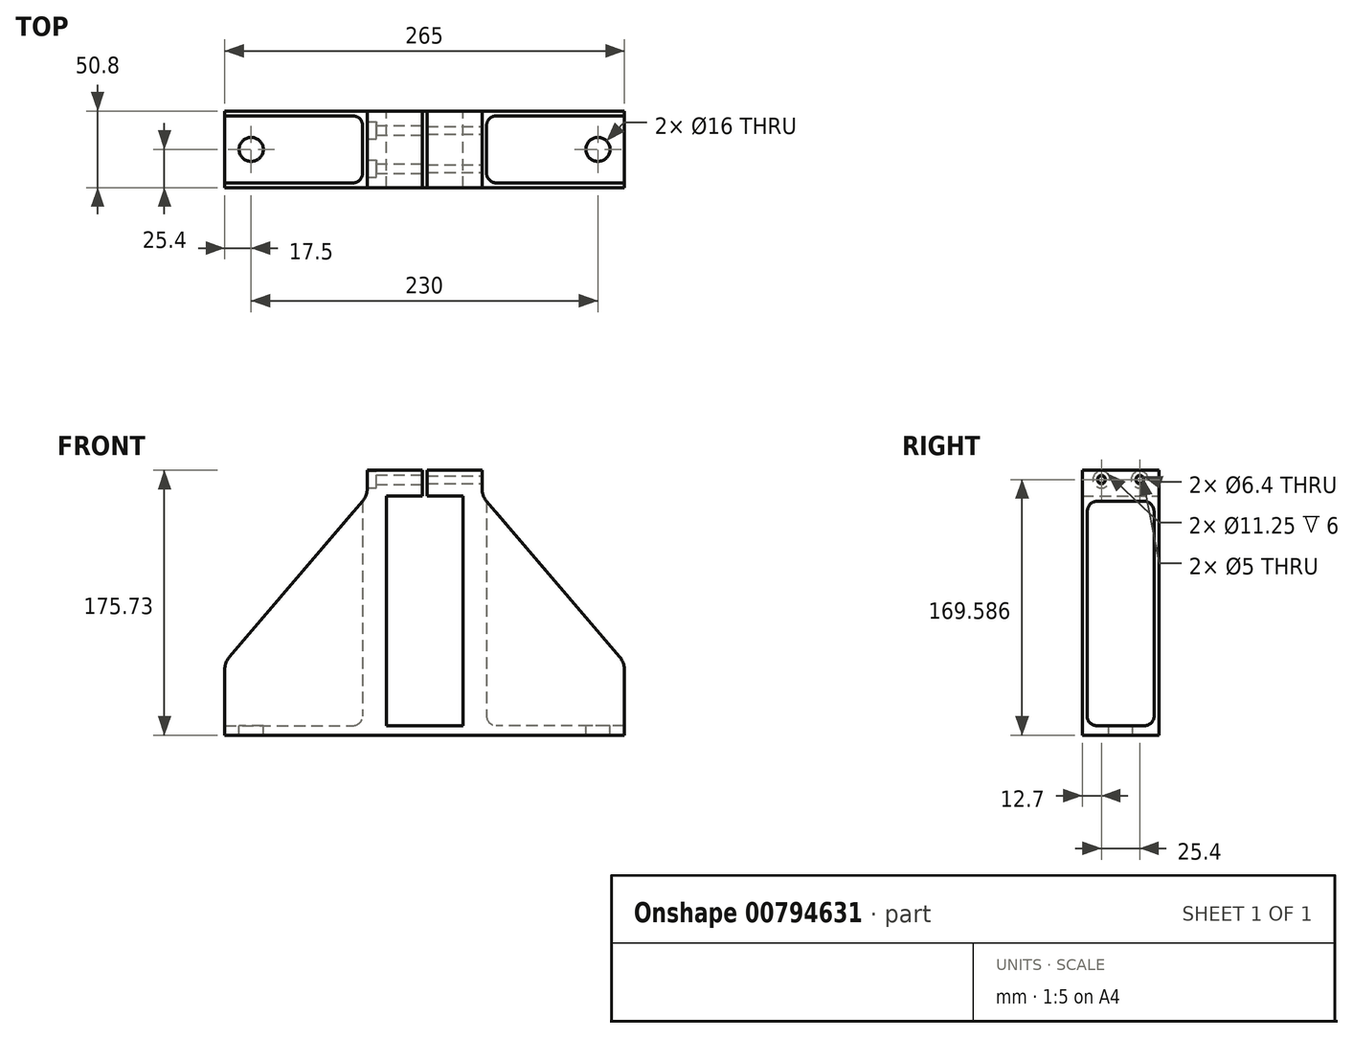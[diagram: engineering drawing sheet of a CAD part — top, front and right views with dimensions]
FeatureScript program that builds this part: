
annotation { "Feature Type Name" : "Feature", "Feature Type Description" : "" }
export const myFeature = defineFeature(function(context is Context, id is Id, definition is map)
    precondition{}
    {
        {
            var Q0;
            Q0=qCreatedBy(makeId("Front.planeOp"),FACE);
            var sketch = newSketch(context, id + "F0", { "sketchPlane" : qUnion([Q0])});
            skLineSegment(sketch, "E0.bottom", {"start": v(25.4, -76.2) * mm, "end": v(-25.4, -76.2) * mm, "construction": true});
            skLineSegment(sketch, "E0.top", {"start": v(25.4, 76.2) * mm, "end": v(1.59, 76.2) * mm, "construction": true});
            skLineSegment(sketch, "E0.left", {"start": v(25.4, -76.2) * mm, "end": v(25.4, 76.2) * mm, "construction": true});
            skLineSegment(sketch, "E0.right", {"start": v(-25.4, -76.2) * mm, "end": v(-25.4, 76.2) * mm, "construction": true});
            skPoint(sketch, "E0.middle", {"position": v(0, 0) * mm});
            skLineSegment(sketch, "E1.bottom", {"start": v(22.22, -73.03) * mm, "end": v(-22.23, -73.03) * mm, "construction": true});
            skLineSegment(sketch, "E1.top", {"start": v(22.23, 73.03) * mm, "end": v(-22.22, 73.03) * mm, "construction": true});
            skLineSegment(sketch, "E1.left", {"start": v(22.22, -73.03) * mm, "end": v(22.23, 73.02) * mm, "construction": true});
            skLineSegment(sketch, "E1.right", {"start": v(-22.23, -73.02) * mm, "end": v(-22.22, 73.03) * mm, "construction": true});
            skLineSegment(sketch, "E2", {"start": v(-115, -34.18) * mm, "end": v(-115, -125.66) * mm, "construction": true});
            skLineSegment(sketch, "E3", {"start": v(115, -25.79) * mm, "end": v(115, -125.66) * mm, "construction": true});
            skLineSegment(sketch, "E4", {"start": v(-43.18, -85.2) * mm, "end": v(50.09, -85.2) * mm, "construction": true});
            skLineSegment(sketch, "E5", {"start": v(50.09, -104.25) * mm, "end": v(-46.8, -104.25) * mm, "construction": true});
            skLineSegment(sketch, "E6", {"start": v(50.09, -85.2) * mm, "end": v(50.09, -104.25) * mm, "construction": true});
            skPoint(sketch, "E7", {"position": v(115, -94.72) * mm});
            skPoint(sketch, "E7.positionSnap0", {"position": v(50.09, -94.72) * mm});
            skLineSegment(sketch, "E8.bottom", {"start": v(132.5, -103.72) * mm, "end": v(97.5, -103.72) * mm, "construction": true});
            skLineSegment(sketch, "E8.top", {"start": v(132.5, -85.72) * mm, "end": v(97.5, -85.72) * mm, "construction": true});
            skLineSegment(sketch, "E8.left", {"start": v(132.5, -103.72) * mm, "end": v(132.5, -85.72) * mm, "construction": true});
            skLineSegment(sketch, "E8.right", {"start": v(97.5, -103.72) * mm, "end": v(97.5, -85.72) * mm, "construction": true});
            skPoint(sketch, "E9", {"position": v(-115, -94.72) * mm});
            skLineSegment(sketch, "E10.bottom", {"start": v(-97.5, -103.72) * mm, "end": v(-132.5, -103.72) * mm, "construction": true});
            skLineSegment(sketch, "E10.top", {"start": v(-97.5, -85.72) * mm, "end": v(-132.5, -85.72) * mm, "construction": true});
            skLineSegment(sketch, "E10.left", {"start": v(-97.5, -103.72) * mm, "end": v(-97.5, -85.72) * mm, "construction": true});
            skLineSegment(sketch, "E10.right", {"start": v(-132.5, -103.72) * mm, "end": v(-132.5, -85.72) * mm, "construction": true});
            skLineSegment(sketch, "E11", {"start": v(107, -85.72) * mm, "end": v(107, -53.22) * mm, "construction": true});
            skLineSegment(sketch, "E12", {"start": v(107, -53.22) * mm, "end": v(123, -53.22) * mm, "construction": true});
            skLineSegment(sketch, "E13", {"start": v(123, -53.22) * mm, "end": v(123, -85.72) * mm, "construction": true});
            skPoint(sketch, "E14", {"position": v(-115, -69.47) * mm});
            skLineSegment(sketch, "E15.bottom", {"start": v(-107, -85.72) * mm, "end": v(-123, -85.72) * mm, "construction": true});
            skLineSegment(sketch, "E15.top", {"start": v(-107, -53.22) * mm, "end": v(-123, -53.22) * mm, "construction": true});
            skLineSegment(sketch, "E15.left", {"start": v(-107, -85.72) * mm, "end": v(-107, -53.22) * mm, "construction": true});
            skLineSegment(sketch, "E15.right", {"start": v(-123, -85.72) * mm, "end": v(-123, -53.22) * mm, "construction": true});
            skLineSegment(sketch, "E16.bottom", {"start": v(-132.5, -82.55) * mm, "end": v(132.5, -82.55) * mm});
            skLineSegment(sketch, "E16.top", {"start": v(-38.1, 93.18) * mm, "end": v(-1.59, 93.18) * mm});
            skLineSegment(sketch, "E16.left", {"start": v(-132.5, -82.55) * mm, "end": v(-132.5, -38.87) * mm});
            skLineSegment(sketch, "E16.right", {"start": v(132.5, -82.55) * mm, "end": v(132.5, -38.87) * mm});
            skLineSegment(sketch, "E17.bottom", {"start": v(-25.4, 76.2) * mm, "end": v(-1.59, 76.2) * mm});
            skLineSegment(sketch, "E17.top", {"start": v(-25.4, -76.2) * mm, "end": v(25.4, -76.2) * mm});
            skLineSegment(sketch, "E17.left", {"start": v(-25.4, 76.2) * mm, "end": v(-25.4, -76.2) * mm});
            skLineSegment(sketch, "E17.right", {"start": v(25.4, 76.2) * mm, "end": v(25.4, -76.2) * mm});
            skLineSegment(sketch, "E18", {"start": v(-129.45, -30.61) * mm, "end": v(-41.15, 72.64) * mm});
            skLineSegment(sketch, "E19", {"start": v(-38.1, 80.9) * mm, "end": v(-38.1, 93.18) * mm});
            skLineSegment(sketch, "E20", {"start": v(38.1, 93.18) * mm, "end": v(38.1, 80.9) * mm});
            skLineSegment(sketch, "E21", {"start": v(41.15, 72.64) * mm, "end": v(129.45, -30.61) * mm});
            skLineSegment(sketch, "E22", {"start": v(0, 76.2) * mm, "end": v(0, 93.18) * mm, "construction": true});
            skLineSegment(sketch, "E23.left", {"start": v(1.59, 76.2) * mm, "end": v(1.59, 93.18) * mm});
            skLineSegment(sketch, "E23.right", {"start": v(-1.59, 76.2) * mm, "end": v(-1.59, 93.18) * mm});
            skPoint(sketch, "E23.middle", {"position": v(0, 84.7) * mm});
            skLineSegment(sketch, "E24.trimOffspring", {"start": v(1.59, 93.18) * mm, "end": v(38.1, 93.18) * mm});
            skLineSegment(sketch, "E25.trimOffspring", {"start": v(-1.59, 76.2) * mm, "end": v(-25.4, 76.2) * mm, "construction": true});
            skLineSegment(sketch, "E26.trimOffspring", {"start": v(1.59, 76.2) * mm, "end": v(25.4, 76.2) * mm});
            skPoint(sketch, "E27.visualSharp", {"position": v(-38.1, 76.2) * mm});
            skArc(sketch, "E27.filletArc", {"start": v(-41.15, 72.64) * mm, "mid": v(-38.89, 76.5) * mm, "end": v(-38.1, 80.9) * mm});
            skPoint(sketch, "E28.visualSharp", {"position": v(38.1, 76.2) * mm});
            skArc(sketch, "E28.filletArc", {"start": v(38.1, 80.9) * mm, "mid": v(38.89, 76.5) * mm, "end": v(41.15, 72.64) * mm});
            skPoint(sketch, "E29.visualSharp", {"position": v(-132.5, -34.17) * mm});
            skArc(sketch, "E29.filletArc", {"start": v(-129.45, -30.61) * mm, "mid": v(-131.71, -34.47) * mm, "end": v(-132.5, -38.87) * mm});
            skPoint(sketch, "E30.visualSharp", {"position": v(132.5, -34.17) * mm});
            skArc(sketch, "E30.filletArc", {"start": v(132.5, -38.87) * mm, "mid": v(131.71, -34.47) * mm, "end": v(129.45, -30.61) * mm});
            skSolve(sketch);
        }
        {
            var Q0;
            Q0=qSketchRegion(id+"F0",true);
            extrude(context, id + "F1", {"entities" : qUnion([Q0]), "depth" : 50.8 * mm, "offsetDistance" : 25 * mm});
        }
        {
            var Q0;
            Q0=makeQuery(id+"F1.opExtrude","SWEPT_FACE",FACE,{"disambiguationData":[OSD([sQuery(id+"F0.wireOp",EDGE,"E19")])]});
            var sketch = newSketch(context, id + "F2", { "sketchPlane" : qUnion([Q0])});
            skLineSegment(sketch, "E31", {"start": v(0, 87.04) * mm, "end": v(50.8, 87.04) * mm, "construction": true});
            skCircle(sketch, "E32", {"center": v(25.4, 87.04) * mm, "radius": 12.7 * mm, "construction": true});
            skPoint(sketch, "E33", {"position": v(12.7, 87.04) * mm});
            skPoint(sketch, "E34", {"position": v(38.1, 87.04) * mm});
            skSolve(sketch);
        }
        {
            var Q0;
            Q0=sQuery(id+"F2.wireOp",VERTEX,"E33");
            var Q1;
            Q1=sQuery(id+"F2.wireOp",VERTEX,"E34");
            var Q2;
            Q2=makeQuery(id+"F1.opExtrude","SWEPT_BODY",BODY,{"disambiguationData":[OSD([sQuery(id+"F0.wireOp",EDGE,"E16.bottom"),sQuery(id+"F0.wireOp",EDGE,"E16.top"),sQuery(id+"F0.wireOp",EDGE,"E16.left"),sQuery(id+"F0.wireOp",EDGE,"E16.right"),sQuery(id+"F0.wireOp",EDGE,"E17.bottom"),sQuery(id+"F0.wireOp",EDGE,"E17.top"),sQuery(id+"F0.wireOp",EDGE,"E17.left"),sQuery(id+"F0.wireOp",EDGE,"E17.right"),sQuery(id+"F0.wireOp",EDGE,"E18"),sQuery(id+"F0.wireOp",EDGE,"E19"),sQuery(id+"F0.wireOp",EDGE,"E20"),sQuery(id+"F0.wireOp",EDGE,"E21"),sQuery(id+"F0.wireOp",EDGE,"E23.left"),sQuery(id+"F0.wireOp",EDGE,"E23.right"),sQuery(id+"F0.wireOp",EDGE,"E24.trimOffspring"),sQuery(id+"F0.wireOp",EDGE,"E26.trimOffspring"),sQuery(id+"F0.wireOp",EDGE,"E27.filletArc"),sQuery(id+"F0.wireOp",EDGE,"E28.filletArc")])]});
            hole(context, id + "F3", {"style" : HoleStyle.C_BORE, "endStyle" : HoleEndStyle.BLIND, "standardTappedOrClearance" : lookupTablePath({ "fit" : "Close", "standard" : "ISO", "size" : "M6", "type" : "Clearance" }), "standardBlindInLast" : lookupTablePath({ "fit" : "Close", "standard" : "ISO", "size" : "M6", "type" : "Clearance" }), "holeDiameter" : 6.4 * mm, "cBoreDiameter" : 11.25 * mm, "cBoreDepth" : 6 * mm, "majorDiameter" : 5 * mm, "holeDepth" : 38.6 * mm, "isTappedThrough" : true, "tappedDepth" : 10.5 * mm, "tapClearance" : 3, "locations" : qUnion([Q0, Q1]), "scope" : qUnion([Q2]), "startStyle" : HoleStartStyle.SKETCH});
        }
        {
            var Q0;
            Q0=makeQuery(id+"F1.opExtrude","SWEPT_FACE",FACE,{"disambiguationData":[OSD([sQuery(id+"F0.wireOp",EDGE,"E17.top")])]});
            var sketch = newSketch(context, id + "F4", { "sketchPlane" : qUnion([Q0])});
            skLineSegment(sketch, "E35.bottom", {"start": v(132.5, -47.62) * mm, "end": v(41.15, -47.63) * mm});
            skLineSegment(sketch, "E35.top", {"start": v(132.5, -3.17) * mm, "end": v(41.15, -3.18) * mm});
            skLineSegment(sketch, "E35.left", {"start": v(132.5, -47.62) * mm, "end": v(132.5, -3.17) * mm});
            skLineSegment(sketch, "E35.right", {"start": v(41.15, -47.62) * mm, "end": v(41.15, -3.18) * mm});
            skLineSegment(sketch, "E36.bottom", {"start": v(-132.5, -3.17) * mm, "end": v(-41.15, -3.17) * mm});
            skLineSegment(sketch, "E36.top", {"start": v(-132.5, -47.62) * mm, "end": v(-41.15, -47.62) * mm});
            skLineSegment(sketch, "E36.left", {"start": v(-132.5, -3.18) * mm, "end": v(-132.5, -47.62) * mm});
            skLineSegment(sketch, "E36.right", {"start": v(-41.15, -3.18) * mm, "end": v(-41.15, -47.62) * mm});
            skSolve(sketch);
        }
        {
            var Q0;
            Q0=qSketchRegion(id+"F4",true);
            extrude(context, id + "F5", {"entities" : qUnion([Q0]), "operationType" : NewBodyOperationType.REMOVE, "depth" : 180.1 * mm, "offsetDistance" : 25 * mm});
        }
        {
            var Q0;
            Q0=makeQuery(id+"F1.opExtrude","SWEPT_FACE",FACE,{"disambiguationData":[OSD([sQuery(id+"F0.wireOp",EDGE,"E16.bottom")])]});
            var sketch = newSketch(context, id + "F6", { "sketchPlane" : qUnion([Q0])});
            skLineSegment(sketch, "E37", {"start": v(-132.5, 25.4) * mm, "end": v(132.5, 25.4) * mm, "construction": true});
            skCircle(sketch, "E38", {"center": v(0, 25.4) * mm, "radius": 115 * mm, "construction": true});
            skPoint(sketch, "E39", {"position": v(-115, 25.4) * mm});
            skPoint(sketch, "E40", {"position": v(115, 25.4) * mm});
            skSolve(sketch);
        }
        {
            var Q0;
            Q0=sQuery(id+"F6.wireOp",VERTEX,"E39");
            var Q1;
            Q1=sQuery(id+"F6.wireOp",VERTEX,"E40");
            var Q2;
            Q2=makeQuery(id+"F1.opExtrude","SWEPT_BODY",BODY,{"disambiguationData":[OSD([sQuery(id+"F0.wireOp",EDGE,"E16.bottom"),sQuery(id+"F0.wireOp",EDGE,"E16.top"),sQuery(id+"F0.wireOp",EDGE,"E16.left"),sQuery(id+"F0.wireOp",EDGE,"E16.right"),sQuery(id+"F0.wireOp",EDGE,"E17.bottom"),sQuery(id+"F0.wireOp",EDGE,"E17.top"),sQuery(id+"F0.wireOp",EDGE,"E17.left"),sQuery(id+"F0.wireOp",EDGE,"E17.right"),sQuery(id+"F0.wireOp",EDGE,"E18"),sQuery(id+"F0.wireOp",EDGE,"E19"),sQuery(id+"F0.wireOp",EDGE,"E20"),sQuery(id+"F0.wireOp",EDGE,"E21"),sQuery(id+"F0.wireOp",EDGE,"E23.left"),sQuery(id+"F0.wireOp",EDGE,"E23.right"),sQuery(id+"F0.wireOp",EDGE,"E24.trimOffspring"),sQuery(id+"F0.wireOp",EDGE,"E26.trimOffspring"),sQuery(id+"F0.wireOp",EDGE,"E27.filletArc"),sQuery(id+"F0.wireOp",EDGE,"E28.filletArc"),sQuery(id+"F0.wireOp",EDGE,"E29.filletArc"),sQuery(id+"F0.wireOp",EDGE,"E30.filletArc")])]});
            hole(context, id + "F7", {"style" : HoleStyle.SIMPLE, "endStyle" : HoleEndStyle.THROUGH, "holeDiameter" : 16 * mm, "majorDiameter" : 5 * mm, "isTappedThrough" : true, "tappedDepth" : 10.5 * mm, "tapClearance" : 3, "locations" : qUnion([Q0, Q1]), "scope" : qUnion([Q2]), "startStyle" : HoleStartStyle.SKETCH});
        }
        {
            var Q0;
            Q0=makeQuery(id+"F5.boolean.opBoolean","COPY",EDGE,{"derivedFrom":makeQuery(id+"F5.opExtrude","CAP_EDGE",EDGE,{"disambiguationData":[OSD([sQuery(id+"F4.wireOp",EDGE,"E35.top")])],"isStart":true})});
            var Q1;
            Q1=makeQuery(id+"F5.boolean.opBoolean","COPY",EDGE,{"derivedFrom":makeQuery(id+"F5.opExtrude","SWEPT_EDGE",EDGE,{"disambiguationData":[OSD([sQuery(id+"F4.wireOp",EDGE,"E35.top"),sQuery(id+"F4.wireOp",EDGE,"E35.right")])]})});
            var Q2;
            Q2=makeQuery(id+"F5.boolean.opBoolean","COPY",EDGE,{"derivedFrom":makeQuery(id+"F5.opExtrude","CAP_EDGE",EDGE,{"disambiguationData":[OSD([sQuery(id+"F4.wireOp",EDGE,"E35.right")])],"isStart":true})});
            var Q3;
            Q3=makeQuery(id+"F5.boolean.opBoolean","COPY",EDGE,{"derivedFrom":makeQuery(id+"F5.opExtrude","CAP_EDGE",EDGE,{"disambiguationData":[OSD([sQuery(id+"F4.wireOp",EDGE,"E35.bottom")])],"isStart":true})});
            var Q4;
            Q4=makeQuery(id+"F5.boolean.opBoolean","COPY",EDGE,{"derivedFrom":makeQuery(id+"F5.opExtrude","SWEPT_EDGE",EDGE,{"disambiguationData":[OSD([sQuery(id+"F4.wireOp",EDGE,"E35.bottom"),sQuery(id+"F4.wireOp",EDGE,"E35.right")])]})});
            var Q5;
            Q5=makeQuery(id+"F5.boolean.opBoolean","COPY",EDGE,{"derivedFrom":makeQuery(id+"F5.opExtrude","CAP_EDGE",EDGE,{"disambiguationData":[OSD([sQuery(id+"F4.wireOp",EDGE,"E36.right")])],"isStart":true})});
            var Q6;
            Q6=makeQuery(id+"F5.boolean.opBoolean","COPY",EDGE,{"derivedFrom":makeQuery(id+"F5.opExtrude","CAP_EDGE",EDGE,{"disambiguationData":[OSD([sQuery(id+"F4.wireOp",EDGE,"E36.top")])],"isStart":true})});
            var Q7;
            Q7=makeQuery(id+"F5.boolean.opBoolean","COPY",EDGE,{"derivedFrom":makeQuery(id+"F5.opExtrude","SWEPT_EDGE",EDGE,{"disambiguationData":[OSD([sQuery(id+"F4.wireOp",EDGE,"E36.top"),sQuery(id+"F4.wireOp",EDGE,"E36.right")])]})});
            var Q8;
            Q8=makeQuery(id+"F5.boolean.opBoolean","COPY",EDGE,{"derivedFrom":makeQuery(id+"F5.opExtrude","CAP_EDGE",EDGE,{"disambiguationData":[OSD([sQuery(id+"F4.wireOp",EDGE,"E36.bottom")])],"isStart":true})});
            var Q9;
            Q9=makeQuery(id+"F5.boolean.opBoolean","COPY",EDGE,{"derivedFrom":makeQuery(id+"F5.opExtrude","SWEPT_EDGE",EDGE,{"disambiguationData":[OSD([sQuery(id+"F4.wireOp",EDGE,"E36.bottom"),sQuery(id+"F4.wireOp",EDGE,"E36.right")])]})});
            fillet(context, id + "F8", {"entities" : qUnion([Q0, Q1, Q2, Q3, Q4, Q5, Q6, Q7, Q8, Q9]), "radius" : 6.35 * mm, "tangentPropagation" : true, "allowEdgeOverflow" : false});
        }
        {
            var Q0;
            Q0=sQuery(id+"F2.wireOp",VERTEX,"E33");
            var Q1;
            Q1=sQuery(id+"F2.wireOp",VERTEX,"E34");
            var Q2;
            Q2=makeQuery(id+"F1.opExtrude","SWEPT_BODY",BODY,{"disambiguationData":[OSD([sQuery(id+"F0.wireOp",EDGE,"E16.bottom"),sQuery(id+"F0.wireOp",EDGE,"E16.top"),sQuery(id+"F0.wireOp",EDGE,"E16.left"),sQuery(id+"F0.wireOp",EDGE,"E16.right"),sQuery(id+"F0.wireOp",EDGE,"E17.bottom"),sQuery(id+"F0.wireOp",EDGE,"E17.top"),sQuery(id+"F0.wireOp",EDGE,"E17.left"),sQuery(id+"F0.wireOp",EDGE,"E17.right"),sQuery(id+"F0.wireOp",EDGE,"E18"),sQuery(id+"F0.wireOp",EDGE,"E19"),sQuery(id+"F0.wireOp",EDGE,"E20"),sQuery(id+"F0.wireOp",EDGE,"E21"),sQuery(id+"F0.wireOp",EDGE,"E23.left"),sQuery(id+"F0.wireOp",EDGE,"E23.right"),sQuery(id+"F0.wireOp",EDGE,"E24.trimOffspring"),sQuery(id+"F0.wireOp",EDGE,"E26.trimOffspring"),sQuery(id+"F0.wireOp",EDGE,"E27.filletArc"),sQuery(id+"F0.wireOp",EDGE,"E28.filletArc"),sQuery(id+"F0.wireOp",EDGE,"E29.filletArc"),sQuery(id+"F0.wireOp",EDGE,"E30.filletArc")])]});
            hole(context, id + "F9", {"style" : HoleStyle.C_BORE, "endStyle" : HoleEndStyle.THROUGH, "standardTappedOrClearance" : lookupTablePath({ "standard" : "ISO", "engagement" : "75%", "pitch" : "1 mm", "size" : "M6", "type" : "Tapped" }), "standardBlindInLast" : lookupTablePath({ "standard" : "ISO", "engagement" : "75%", "pitch" : "1 mm", "size" : "M6", "type" : "Tapped" }), "holeDiameter" : 5 * mm, "cBoreDiameter" : 11.25 * mm, "cBoreDepth" : 6 * mm, "majorDiameter" : 6 * mm, "showTappedDepth" : true, "isTappedThrough" : true, "tappedDepth" : 10.5 * mm, "tapClearance" : 3, "locations" : qUnion([Q0, Q1]), "scope" : qUnion([Q2]), "startStyle" : HoleStartStyle.SKETCH});
        }
    });
